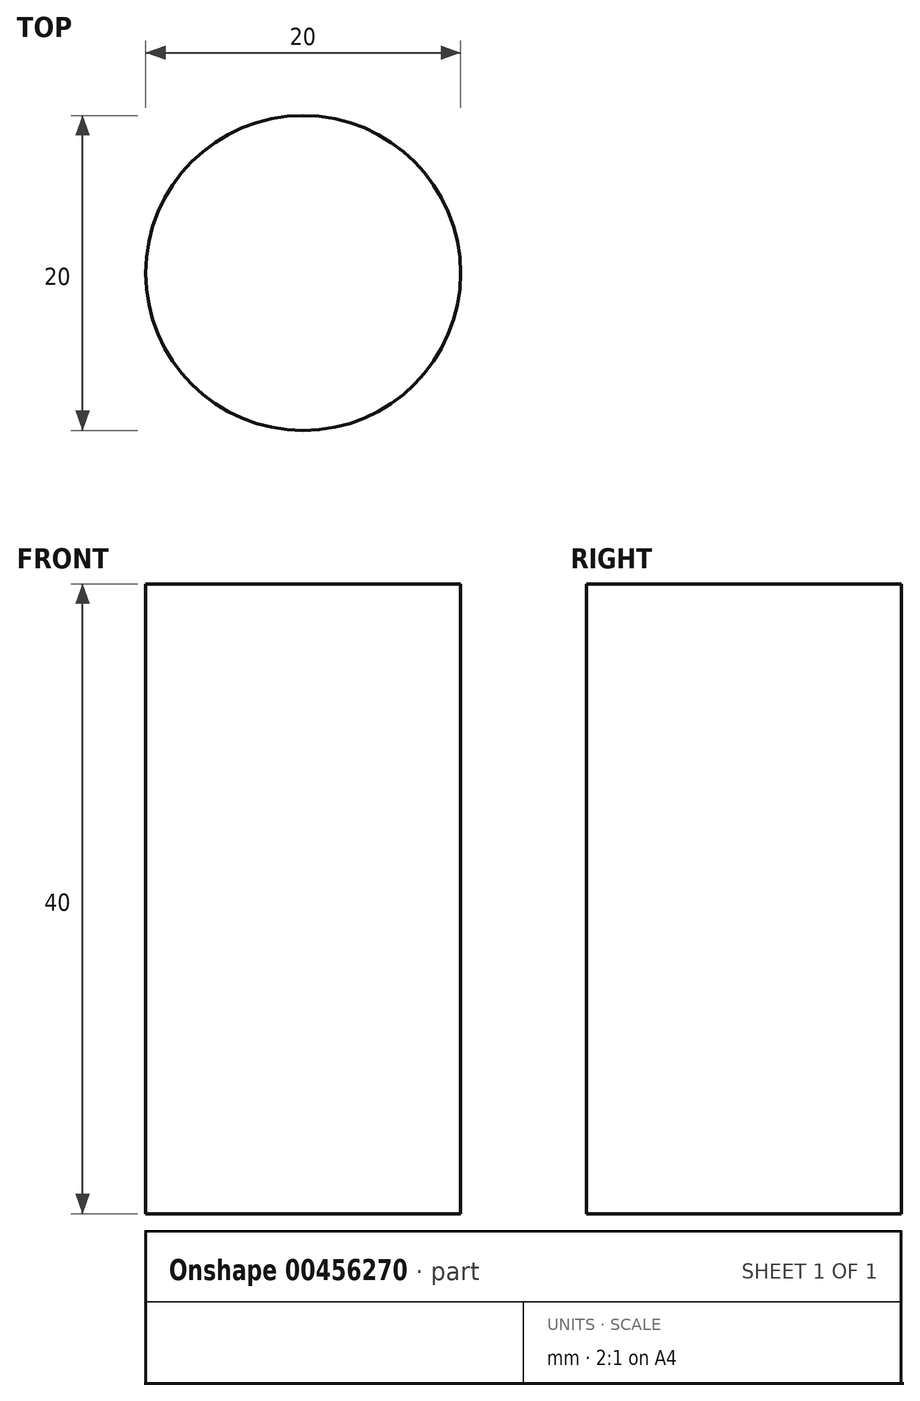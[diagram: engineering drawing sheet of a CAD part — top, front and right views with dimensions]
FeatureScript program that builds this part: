
annotation { "Feature Type Name" : "Feature", "Feature Type Description" : "" }
export const myFeature = defineFeature(function(context is Context, id is Id, definition is map)
    precondition{}
    {
        {
            var Q0;
            Q0=qCreatedBy(makeId("Top.planeOp"),FACE);
            var sketch = newSketch(context, id + "F0", { "sketchPlane" : qUnion([Q0])});
            skCircle(sketch, "E0", {"center": v(0, 0) * mm, "radius": 10 * mm});
            skSolve(sketch);
        }
        {
            var Q0;
            Q0=makeQuery(id+"F0.imprint","IMPRINT",FACE,{"disambiguationData":[TD([[makeQuery(id+"F0.imprint","IMPRINT",EDGE,{"derivedFrom":sQuery(id+"F0.wireOp",EDGE,"E0")}),1.0]])]});
            extrude(context, id + "F1", {"entities" : qUnion([Q0]), "depth" : 40 * mm});
        }
    });
